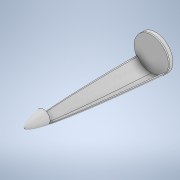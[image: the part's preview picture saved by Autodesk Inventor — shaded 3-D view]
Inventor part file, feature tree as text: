
AUTODESK INVENTOR PART (.ipt)
format: ipt  version: 2020.3 (Build 243373000, 373)  size: 222,208 bytes
history: native  units: mm
features: sketch x1, revolve x1, extrude x1
ambient origin geometry x8: Origin, YZ Plane, XZ Plane, XY Plane, X Axis, Y Axis, Z Axis, Center Point
bodies: Body1 (feature_tree)
feature tree (3):
  sketch  "Sketch2"  dims[d51=25.9mm d52=5.0mm d53=0.9mm d54=2.0mm d55=25.9mm d56=5.0mm d57=0.9mm d58=170.0mm d59=200.0mm d60=25.0mm d61=25.0mm d62=198.2mm d64=25.0mm d67=2.0mm d68=170.0mm d69=5.0mm d70=8.0mm d71=170.0mm d72=15.232132mm d73=360.0deg d74=60.0mm d75=0.0mm d7=0.5mm d8=0.872665mm d9=0.5mm d10=0.872665mm]
  revolve  "Revolution5"  [1 undecoded]
  extrude  "Extrusion4"  Depth=0.9mm
note: 1 required parameter value undecoded (feature->parameter linkage not recoverable at this tier; creation-order binding heuristic only, values carry confidence <= 0.55)
